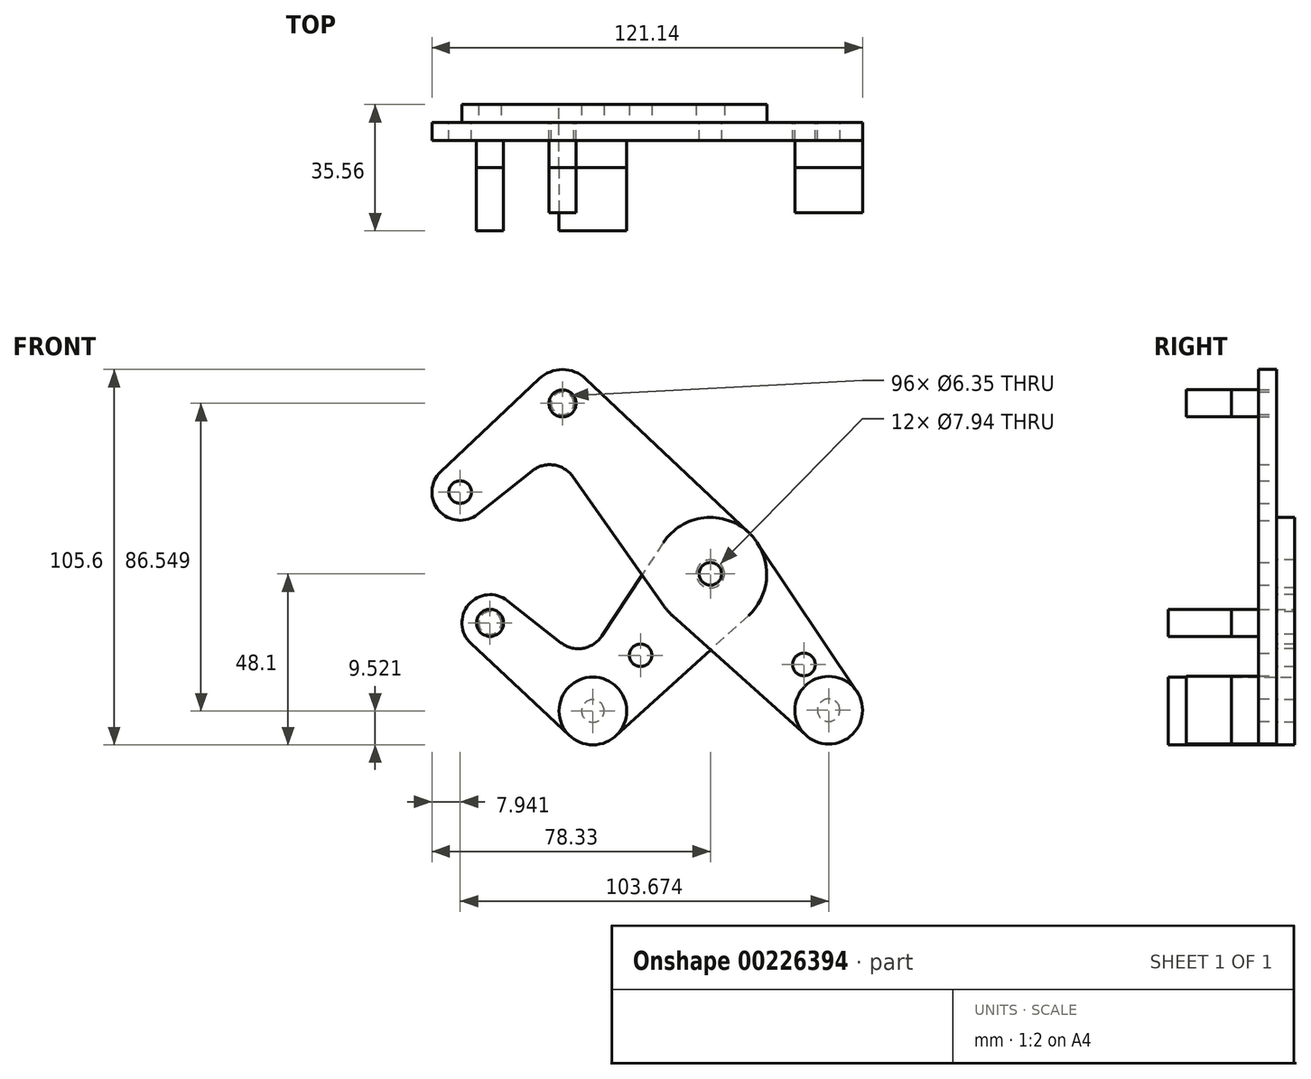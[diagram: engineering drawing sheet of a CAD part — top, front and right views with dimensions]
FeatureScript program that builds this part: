
annotation { "Feature Type Name" : "Feature", "Feature Type Description" : "" }
export const myFeature = defineFeature(function(context is Context, id is Id, definition is map)
    precondition{}
    {
        {
            var Q0;
            Q0=qCreatedBy(makeId("Front.planeOp"),FACE);
            var sketch = newSketch(context, id + "F0", { "sketchPlane" : qUnion([Q0])});
            skLineSegment(sketch, "E0", {"start": v(-41.6, 47.97) * mm, "end": v(41.6, -47.97) * mm, "construction": true});
            skCircle(sketch, "E1", {"center": v(0, 0) * mm, "radius": 3.18 * mm});
            skCircle(sketch, "E2", {"center": v(33.29, -38.38) * mm, "radius": 3.18 * mm});
            skCircle(sketch, "E3", {"center": v(-41.6, 47.97) * mm, "radius": 3.18 * mm});
            skCircle(sketch, "E4", {"center": v(-70.39, 23) * mm, "radius": 3.18 * mm});
            skLineSegment(sketch, "E5", {"start": v(-41.6, 47.97) * mm, "end": v(-70.39, 23) * mm, "construction": true});
            skCircle(sketch, "E6", {"center": v(33.29, -38.38) * mm, "radius": 9.53 * mm});
            skCircle(sketch, "E7", {"center": v(-70.39, 23) * mm, "radius": 7.94 * mm});
            skCircle(sketch, "E8", {"center": v(-41.6, 47.97) * mm, "radius": 9.53 * mm});
            skLineSegment(sketch, "E9", {"start": v(-75.83, 28.78) * mm, "end": v(-48.14, 54.9) * mm});
            skLineSegment(sketch, "E10", {"start": v(-65.44, 16.8) * mm, "end": v(-50.15, 28.98) * mm});
            skCircle(sketch, "E11", {"center": v(0, 0) * mm, "radius": 15.88 * mm});
            skLineSegment(sketch, "E12", {"start": v(-35.07, 54.9) * mm, "end": v(10.9, 11.55) * mm});
            skLineSegment(sketch, "E13", {"start": v(-38.72, 27.35) * mm, "end": v(-12.97, -9.15) * mm});
            skLineSegment(sketch, "E14", {"start": v(-10.6, -11.82) * mm, "end": v(26.93, -45.47) * mm});
            skLineSegment(sketch, "E15", {"start": v(13.2, 8.82) * mm, "end": v(41.2, -33.08) * mm});
            skArc(sketch, "E16.filletArc", {"start": v(-38.72, 27.35) * mm, "mid": v(-44.08, 30.63) * mm, "end": v(-50.15, 28.98) * mm});
            skLineSegment(sketch, "E17", {"start": v(0, 0) * mm, "end": v(-33.05, -38.58) * mm, "construction": true});
            skLineSegment(sketch, "E18", {"start": v(-33.05, -38.58) * mm, "end": v(-61.98, -13.8) * mm, "construction": true});
            skCircle(sketch, "E19", {"center": v(-61.98, -13.8) * mm, "radius": 3.18 * mm});
            skCircle(sketch, "E20", {"center": v(-33.05, -38.58) * mm, "radius": 3.18 * mm});
            skCircle(sketch, "E21", {"center": v(-61.98, -13.8) * mm, "radius": 7.94 * mm});
            skCircle(sketch, "E22", {"center": v(-33.05, -38.58) * mm, "radius": 9.53 * mm});
            skLineSegment(sketch, "E23", {"start": v(-57.08, -7.55) * mm, "end": v(-42.08, -19.35) * mm});
            skLineSegment(sketch, "E24", {"start": v(-67.4, -19.6) * mm, "end": v(-39.54, -45.55) * mm});
            skLineSegment(sketch, "E25", {"start": v(-13.25, 8.74) * mm, "end": v(-30.55, -17.48) * mm});
            skLineSegment(sketch, "E26", {"start": v(10.67, -11.75) * mm, "end": v(-26.65, -45.63) * mm});
            skArc(sketch, "E27.filletArc", {"start": v(-42.08, -19.35) * mm, "mid": v(-35.9, -20.95) * mm, "end": v(-30.55, -17.48) * mm});
            skCircle(sketch, "E28", {"center": v(-19.62, -22.9) * mm, "radius": 3.18 * mm});
            skCircle(sketch, "E29", {"center": v(26.32, -25.5) * mm, "radius": 3.18 * mm});
            skLineSegment(sketch, "E30", {"start": v(26.32, -25.5) * mm, "end": v(23.92, -27.58) * mm, "construction": true});
            skCircle(sketch, "E31", {"center": v(0, 0) * mm, "radius": 3.97 * mm});
            skSolve(sketch);
        }
        {
            var Q0;
            Q0=qCreatedBy(makeId("Front.planeOp"),FACE);
            cPlane(context, id + "F1", {"entities" : qUnion([Q0]), "cplaneType" : CPlaneType.OFFSET, "offset" : 12.7 * mm, "width" : 254 * mm, "height" : 254 * mm});
        }
        {
            var Q0;
            Q0=makeQuery(id+"F0.imprint","IMPRINT",FACE,{"disambiguationData":[TD([[makeQuery(id+"F0.imprint","IMPRINT",EDGE,{"derivedFrom":sQuery(id+"F0.wireOp",EDGE,"E4")}),-1.0]])]});
            var Q1;
            {var subQ1=sQuery(id+"F0.wireOp",EDGE,"E9");Q1=makeQuery(id+"F0.imprint","IMPRINT",FACE,{"disambiguationData":[TD([[makeQuery(id+"F0.imprint","IMPRINT",EDGE,{"derivedFrom":subQ1}),-1.0]])]});}
            var Q2;
            Q2=makeQuery(id+"F0.imprint","IMPRINT",FACE,{"disambiguationData":[TD([[makeQuery(id+"F0.imprint","IMPRINT",EDGE,{"derivedFrom":sQuery(id+"F0.wireOp",EDGE,"E3")}),-1.0]])]});
            var Q3;
            Q3=makeQuery(id+"F0.imprint","IMPRINT",FACE,{"disambiguationData":[TD([[makeQuery(id+"F0.imprint","IMPRINT",EDGE,{"derivedFrom":sQuery(id+"F0.wireOp",EDGE,"E31")}),-1.0]])]});
            var Q4;
            {var subQ0=sQuery(id+"F0.wireOp",EDGE,"E13");var subQ1=sQuery(id+"F0.wireOp",EDGE,"E11");var subQ2=makeQuery(id+"F0.imprint","INTERSECT",VERTEX,{"derivedFrom":[subQ1,subQ0]});Q4=makeQuery(id+"F0.imprint","IMPRINT",FACE,{"disambiguationData":[TD([[makeQuery(id+"F0.imprint","IMPRINT",EDGE,{"disambiguationData":[TD([[subQ2,1.0]])],"derivedFrom":subQ1}),-1.0]])]});}
            var Q5;
            {var subQ0=sQuery(id+"F0.wireOp",EDGE,"E14");var subQ1=sQuery(id+"F0.wireOp",EDGE,"E11");var subQ2=makeQuery(id+"F0.imprint","INTERSECT",VERTEX,{"derivedFrom":[subQ1,subQ0]});Q5=makeQuery(id+"F0.imprint","IMPRINT",FACE,{"disambiguationData":[TD([[makeQuery(id+"F0.imprint","IMPRINT",EDGE,{"disambiguationData":[TD([[subQ2,-1.0]])],"derivedFrom":subQ1}),-1.0]])]});}
            var Q6;
            {var subQ0=sQuery(id+"F0.wireOp",EDGE,"E15");Q6=makeQuery(id+"F0.imprint","IMPRINT",FACE,{"disambiguationData":[TD([[makeQuery(id+"F0.imprint","IMPRINT",EDGE,{"derivedFrom":subQ0}),-1.0]])]});}
            var Q7;
            Q7=makeQuery(id+"F0.imprint","IMPRINT",FACE,{"disambiguationData":[TD([[makeQuery(id+"F0.imprint","IMPRINT",EDGE,{"derivedFrom":sQuery(id+"F0.wireOp",EDGE,"E2")}),-1.0]])]});
            var Q8;
            Q8=makeQuery(id+"F0.imprint","IMPRINT",FACE,{"disambiguationData":[TD([[makeQuery(id+"F0.imprint","IMPRINT",EDGE,{"derivedFrom":sQuery(id+"F0.wireOp",EDGE,"E1")}),-1.0]])]});
            extrude(context, id + "F2", {"entities" : qUnion([Q0, Q1, Q2, Q3, Q4, Q5, Q6, Q7, Q8]), "depth" : 5.08 * mm});
        }
        {
            var Q0;
            Q0=makeQuery(id+"F0.imprint","IMPRINT",FACE,{"disambiguationData":[TD([[makeQuery(id+"F0.imprint","IMPRINT",EDGE,{"derivedFrom":sQuery(id+"F0.wireOp",EDGE,"E31")}),-1.0]])]});
            var Q1;
            {var subQ0=sQuery(id+"F0.wireOp",EDGE,"E14");var subQ1=sQuery(id+"F0.wireOp",EDGE,"E11");var subQ2=makeQuery(id+"F0.imprint","INTERSECT",VERTEX,{"derivedFrom":[subQ1,subQ0]});Q1=makeQuery(id+"F0.imprint","IMPRINT",FACE,{"disambiguationData":[TD([[makeQuery(id+"F0.imprint","IMPRINT",EDGE,{"disambiguationData":[TD([[subQ2,-1.0]])],"derivedFrom":subQ1}),-1.0]])]});}
            var Q2;
            {var subQ10=sQuery(id+"F0.wireOp",EDGE,"E23");Q2=makeQuery(id+"F0.imprint","IMPRINT",FACE,{"disambiguationData":[TD([[makeQuery(id+"F0.imprint","IMPRINT",EDGE,{"derivedFrom":subQ10}),-1.0]])]});}
            var Q3;
            {var subQ0=sQuery(id+"F0.wireOp",EDGE,"E13");var subQ1=sQuery(id+"F0.wireOp",EDGE,"E11");var subQ2=makeQuery(id+"F0.imprint","INTERSECT",VERTEX,{"derivedFrom":[subQ1,subQ0]});Q3=makeQuery(id+"F0.imprint","IMPRINT",FACE,{"disambiguationData":[TD([[makeQuery(id+"F0.imprint","IMPRINT",EDGE,{"disambiguationData":[TD([[subQ2,1.0]])],"derivedFrom":subQ1}),-1.0]])]});}
            var Q4;
            Q4=makeQuery(id+"F0.imprint","IMPRINT",FACE,{"disambiguationData":[TD([[makeQuery(id+"F0.imprint","IMPRINT",EDGE,{"derivedFrom":sQuery(id+"F0.wireOp",EDGE,"E19")}),-1.0]])]});
            var Q5;
            Q5=makeQuery(id+"F0.imprint","IMPRINT",FACE,{"disambiguationData":[TD([[makeQuery(id+"F0.imprint","IMPRINT",EDGE,{"derivedFrom":sQuery(id+"F0.wireOp",EDGE,"E20")}),-1.0]])]});
            extrude(context, id + "F3", {"entities" : qUnion([Q0, Q1, Q2, Q3, Q4, Q5]), "oppositeDirection" : true, "depth" : 5.08 * mm});
        }
        {
            var Q0;
            Q0=makeQuery(id+"F2.opExtrude","CAP_FACE",FACE,{"disambiguationData":[OSD([sQuery(id+"F0.wireOp",EDGE,"E1"),sQuery(id+"F0.wireOp",EDGE,"E2"),sQuery(id+"F0.wireOp",EDGE,"E3"),sQuery(id+"F0.wireOp",EDGE,"E4"),sQuery(id+"F0.wireOp",EDGE,"E6"),sQuery(id+"F0.wireOp",EDGE,"E7"),sQuery(id+"F0.wireOp",EDGE,"E8"),sQuery(id+"F0.wireOp",EDGE,"E9"),sQuery(id+"F0.wireOp",EDGE,"E10"),sQuery(id+"F0.wireOp",EDGE,"E11"),sQuery(id+"F0.wireOp",EDGE,"E12"),sQuery(id+"F0.wireOp",EDGE,"E13"),sQuery(id+"F0.wireOp",EDGE,"E14"),sQuery(id+"F0.wireOp",EDGE,"E15"),sQuery(id+"F0.wireOp",EDGE,"E16.filletArc"),sQuery(id+"F0.wireOp",EDGE,"E29")])],"isStart":true});
            var sketch = newSketch(context, id + "F4", { "sketchPlane" : qUnion([Q0])});
            skCircle(sketch, "E32", {"center": v(41.6, 47.97) * mm, "radius": 3.81 * mm});
            skCircle(sketch, "E33.0", {"center": v(-33.29, -38.38) * mm, "radius": 9.53 * mm});
            skSolve(sketch);
        }
        {
            var Q0;
            Q0=makeQuery(id+"F3.opExtrude","CAP_FACE",FACE,{"disambiguationData":[OSD([sQuery(id+"F0.wireOp",EDGE,"E11"),sQuery(id+"F0.wireOp",EDGE,"E19"),sQuery(id+"F0.wireOp",EDGE,"E20"),sQuery(id+"F0.wireOp",EDGE,"E21"),sQuery(id+"F0.wireOp",EDGE,"E22"),sQuery(id+"F0.wireOp",EDGE,"E23"),sQuery(id+"F0.wireOp",EDGE,"E24"),sQuery(id+"F0.wireOp",EDGE,"E25"),sQuery(id+"F0.wireOp",EDGE,"E26"),sQuery(id+"F0.wireOp",EDGE,"E27.filletArc"),sQuery(id+"F0.wireOp",EDGE,"E28"),sQuery(id+"F0.wireOp",EDGE,"E31")])],"isStart":false});
            var sketch = newSketch(context, id + "F5", { "sketchPlane" : qUnion([Q0])});
            skCircle(sketch, "E34", {"center": v(61.98, -13.8) * mm, "radius": 3.81 * mm});
            skCircle(sketch, "E35.0", {"center": v(33.05, -38.58) * mm, "radius": 9.53 * mm});
            skSolve(sketch);
        }
        {
            var Q0;
            Q0=qSketchRegion(id+"F4",true);
            var Q1;
            Q1=qSketchRegion(id+"F5",true);
            var Q2;
            Q2=qCreatedBy(id+"F1.planeOp",FACE);
            extrude(context, id + "F6", {"entities" : qUnion([Q0, Q1]), "endBound" : BoundingType.UP_TO_SURFACE, "oppositeDirection" : true, "endBoundEntityFace" : qUnion([Q2]), "depth" : 25.4 * mm});
        }
        {
            var Q0;
            Q0=makeQuery(id+"F6.opExtrude","SWEPT_BODY",BODY,{"disambiguationData":[OSD([sQuery(id+"F4.wireOp",EDGE,"E32")])]});
            var Q1;
            Q1=makeQuery(id+"F6.opExtrude","SWEPT_BODY",BODY,{"disambiguationData":[OSD([sQuery(id+"F4.wireOp",EDGE,"E33.0")])]});
            var Q2;
            Q2=makeQuery(id+"F6.opExtrude","SWEPT_BODY",BODY,{"disambiguationData":[OSD([sQuery(id+"F5.wireOp",EDGE,"E34")])]});
            var Q3;
            Q3=makeQuery(id+"F6.opExtrude","SWEPT_BODY",BODY,{"disambiguationData":[OSD([sQuery(id+"F5.wireOp",EDGE,"E35.0")])]});
            var Q4;
            Q4=qCreatedBy(id+"F1.planeOp",FACE);
            mirror(context, id + "F7", {"entities" : qUnion([Q0, Q1, Q2, Q3]), "mirrorPlane" : qUnion([Q4])});
        }
    });
